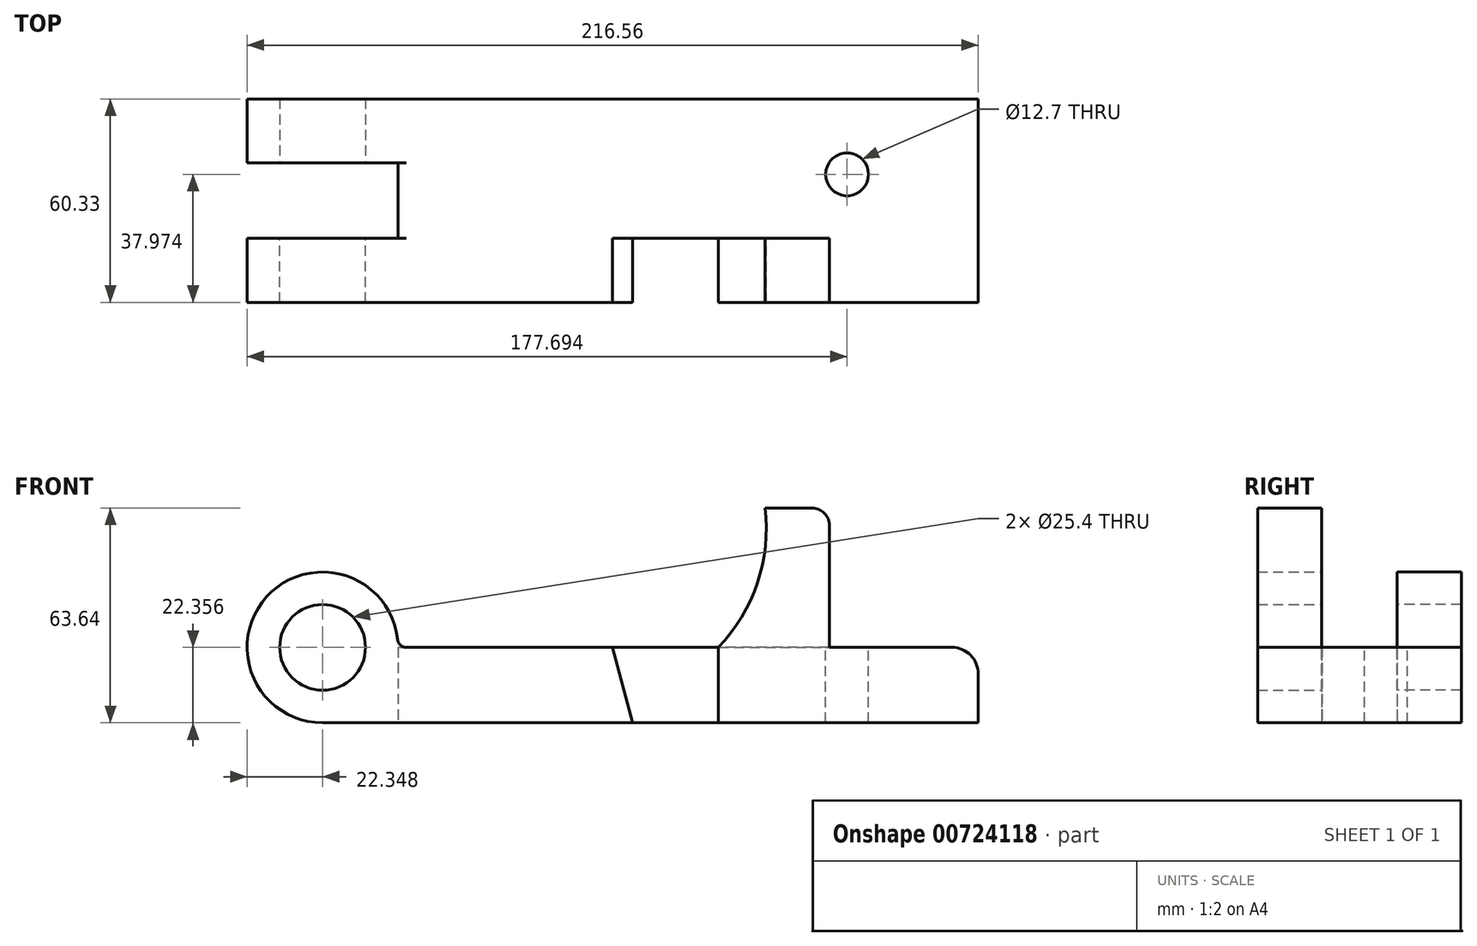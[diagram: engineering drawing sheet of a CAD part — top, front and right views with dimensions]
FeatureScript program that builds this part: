
annotation { "Feature Type Name" : "Feature", "Feature Type Description" : "" }
export const myFeature = defineFeature(function(context is Context, id is Id, definition is map)
    precondition{}
    {
        {
            var Q0;
            Q0=qCreatedBy(makeId("Front.planeOp"),FACE);
            var sketch = newSketch(context, id + "F0", { "sketchPlane" : qUnion([Q0])});
            skLineSegment(sketch, "E0.bottom", {"start": v(-66.8, 11.18) * mm, "end": v(79.5, 11.18) * mm});
            skLineSegment(sketch, "E0.top", {"start": v(-79.5, -11.18) * mm, "end": v(79.5, -11.18) * mm});
            skLineSegment(sketch, "E0.left", {"start": v(-79.5, -1.52) * mm, "end": v(-79.5, -11.18) * mm});
            skPoint(sketch, "E0.middle", {"position": v(0, 0) * mm});
            skArc(sketch, "E1", {"start": v(-57.15, 11.18) * mm, "mid": v(-95.3, 26.98) * mm, "end": v(-79.5, -11.18) * mm});
            skCircle(sketch, "E2", {"center": v(-79.5, 11.18) * mm, "radius": 12.7 * mm});
            skLineSegment(sketch, "E3", {"start": v(-79.5, -1.52) * mm, "end": v(-79.5, 11.18) * mm, "construction": true});
            skArc(sketch, "E4", {"start": v(-79.5, -11.18) * mm, "mid": v(-63.7, -4.63) * mm, "end": v(-57.15, 11.18) * mm});
            skLineSegment(sketch, "E5", {"start": v(6.35, 11.18) * mm, "end": v(12.34, -11.18) * mm});
            skLineSegment(sketch, "E6", {"start": v(37.74, 11.18) * mm, "end": v(37.74, -11.18) * mm});
            skLineSegment(sketch, "E7.bottom", {"start": v(37.74, 11.18) * mm, "end": v(70.59, 11.18) * mm});
            skLineSegment(sketch, "E7.right", {"start": v(70.59, 11.18) * mm, "end": v(70.59, 52.46) * mm});
            skLineSegment(sketch, "E8", {"start": v(79.5, 11.18) * mm, "end": v(114.7, 11.18) * mm});
            skLineSegment(sketch, "E9", {"start": v(114.7, 11.18) * mm, "end": v(114.7, -11.18) * mm});
            skLineSegment(sketch, "E10", {"start": v(114.7, -11.18) * mm, "end": v(79.5, -11.18) * mm});
            skPoint(sketch, "E11", {"position": v(-101.85, 11.18) * mm});
            skLineSegment(sketch, "E12", {"start": v(70.59, 52.46) * mm, "end": v(51.54, 52.46) * mm});
            skArc(sketch, "E13", {"start": v(37.74, 11.18) * mm, "mid": v(49.29, 30.26) * mm, "end": v(51.54, 52.46) * mm});
            skSolve(sketch);
        }
        {
            var Q0;
            Q0 = qSketchRegion(id + "F0", true);
            extrude(context, id + "F1", {"entities" : qUnion([Q0]), "depth" : 19 * mm, "offsetDistance" : 25.4 * mm});
        }
        {
            var Q0;
            {var subQ0=sQuery(id+"F0.wireOp",EDGE,"E4");Q0=makeQuery(id+"F0.imprint","IMPRINT",FACE,{"disambiguationData":[TD([[makeQuery(id+"F0.imprint","IMPRINT",EDGE,{"derivedFrom":subQ0}),-1.0]])]});}
            var sketch = newSketch(context, id + "F2", { "sketchPlane" : qUnion([Q0])});
            skLineSegment(sketch, "E14.bottom", {"start": v(114.7, 11.18) * mm, "end": v(-57.17, 11.18) * mm});
            skLineSegment(sketch, "E14.top", {"start": v(114.7, -11.17) * mm, "end": v(-57.17, -11.17) * mm});
            skLineSegment(sketch, "E14.left", {"start": v(114.7, 11.18) * mm, "end": v(114.7, -11.17) * mm});
            skLineSegment(sketch, "E14.right", {"start": v(-57.17, 11.18) * mm, "end": v(-57.17, -11.17) * mm});
            skSolve(sketch);
        }
        {
            var Q0;
            Q0 = qSketchRegion(id + "F2", true);
            extrude(context, id + "F3", {"entities" : qUnion([Q0]), "operationType" : NewBodyOperationType.ADD, "oppositeDirection" : true, "depth" : 11.16 * mm, "offsetDistance" : 25.4 * mm});
        }
        {
            var Q0;
            Q0=makeQuery(id+"F3.opExtrude","CAP_FACE",FACE,{"disambiguationData":[OSD([sQuery(id+"F2.wireOp",EDGE,"E14.bottom"),sQuery(id+"F2.wireOp",EDGE,"E14.top"),sQuery(id+"F2.wireOp",EDGE,"E14.left"),sQuery(id+"F2.wireOp",EDGE,"E14.right")])],"isStart":false});
            cPlane(context, id + "F4", {"entities" : qUnion([Q0]), "cplaneType" : CPlaneType.OFFSET, "offset" : 0 * mm, "width" : 152.4 * mm, "height" : 152.4 * mm});
        }
        {
            var Q0;
            Q0=makeQuery(id+"F1.opExtrude","SWEPT_BODY",BODY,{"disambiguationData":[OSD([sQuery(id+"F0.wireOp",EDGE,"E0.bottom"),sQuery(id+"F0.wireOp",EDGE,"E0.top"),sQuery(id+"F0.wireOp",EDGE,"E1"),sQuery(id+"F0.wireOp",EDGE,"E2"),sQuery(id+"F0.wireOp",EDGE,"E7.right"),sQuery(id+"F0.wireOp",EDGE,"E8"),sQuery(id+"F0.wireOp",EDGE,"E9"),sQuery(id+"F0.wireOp",EDGE,"E10"),sQuery(id+"F0.wireOp",EDGE,"E12"),sQuery(id+"F0.wireOp",EDGE,"E13")])]});
            var Q1;
            Q1=makeQuery(id+"F3.opExtrude","SWEPT_BODY",BODY,{"disambiguationData":[OSD([sQuery(id+"F2.wireOp",EDGE,"E14.bottom"),sQuery(id+"F2.wireOp",EDGE,"E14.top"),sQuery(id+"F2.wireOp",EDGE,"E14.left"),sQuery(id+"F2.wireOp",EDGE,"E14.right")])]});
            var Q2;
            Q2=qCreatedBy(id+"F4.planeOp",FACE);
            mirror(context, id + "F5", {"operationType" : NewBodyOperationType.ADD, "entities" : qUnion([Q0, Q1]), "mirrorPlane" : qUnion([Q2])});
        }
        {
            var Q0;
            Q0=makeQuery(id+"F5.opPattern","COPY",FACE,{"derivedFrom":makeQuery(id+"F1.opExtrude","CAP_FACE",FACE,{"disambiguationData":[OSD([sQuery(id+"F0.wireOp",EDGE,"E0.bottom"),sQuery(id+"F0.wireOp",EDGE,"E0.top"),sQuery(id+"F0.wireOp",EDGE,"E1"),sQuery(id+"F0.wireOp",EDGE,"E2"),sQuery(id+"F0.wireOp",EDGE,"E7.right"),sQuery(id+"F0.wireOp",EDGE,"E8"),sQuery(id+"F0.wireOp",EDGE,"E9"),sQuery(id+"F0.wireOp",EDGE,"E10"),sQuery(id+"F0.wireOp",EDGE,"E12"),sQuery(id+"F0.wireOp",EDGE,"E13")])],"isStart":false}),"instanceName":"1"});
            var sketch = newSketch(context, id + "F6", { "sketchPlane" : qUnion([Q0])});
            skLineSegment(sketch, "E15.bottom", {"start": v(-70.59, 52.46) * mm, "end": v(-34.03, 52.46) * mm});
            skLineSegment(sketch, "E15.top", {"start": v(-70.59, 11.18) * mm, "end": v(-34.03, 11.18) * mm});
            skLineSegment(sketch, "E15.left", {"start": v(-70.59, 52.46) * mm, "end": v(-70.59, 11.18) * mm});
            skLineSegment(sketch, "E15.right", {"start": v(-34.03, 52.46) * mm, "end": v(-34.03, 11.18) * mm});
            skSolve(sketch);
        }
        {
            var Q0;
            Q0 = qSketchRegion(id + "F6", true);
            extrude(context, id + "F7", {"entities" : qUnion([Q0]), "operationType" : NewBodyOperationType.REMOVE, "oppositeDirection" : true, "depth" : 25.4 * mm, "offsetDistance" : 25.4 * mm});
        }
        {
            var Q0;
            Q0=makeQuery(id+"F1.opExtrude","SWEPT_EDGE",EDGE,{"disambiguationData":[OSD([sQuery(id+"F0.wireOp",EDGE,"E7.right"),sQuery(id+"F0.wireOp",EDGE,"E12")])]});
            fillet(context, id + "F8", {"entities" : qUnion([Q0]), "radius" : 5.08 * mm, "tangentPropagation" : true, "allowEdgeOverflow" : false});
        }
        {
            var Q0;
            Q0=makeQuery(id+"F5.opPattern","COPY",EDGE,{"derivedFrom":makeQuery(id+"F1.opExtrude","SWEPT_EDGE",EDGE,{"disambiguationData":[OSD([sQuery(id+"F0.wireOp",EDGE,"E8"),sQuery(id+"F0.wireOp",EDGE,"E9")])]}),"instanceName":"1"});
            fillet(context, id + "F9", {"entities" : qUnion([Q0]), "radius" : 7.87 * mm, "tangentPropagation" : true, "allowEdgeOverflow" : false});
        }
        {
            var Q0;
            Q0=makeQuery(id+"F1.opExtrude","SWEPT_EDGE",EDGE,{"disambiguationData":[OSD([sQuery(id+"F0.wireOp",EDGE,"E0.bottom"),sQuery(id+"F0.wireOp",EDGE,"E1"),sQuery(id+"F0.wireOp",EDGE,"E4")])]});
            fillet(context, id + "F10", {"entities" : qUnion([Q0]), "radius" : 2.54 * mm, "tangentPropagation" : true, "allowEdgeOverflow" : false});
        }
        {
            var Q0;
            Q0=makeQuery(id+"F5.opPattern","COPY",EDGE,{"derivedFrom":makeQuery(id+"F1.opExtrude","SWEPT_EDGE",EDGE,{"disambiguationData":[OSD([sQuery(id+"F0.wireOp",EDGE,"E0.bottom"),sQuery(id+"F0.wireOp",EDGE,"E1"),sQuery(id+"F0.wireOp",EDGE,"E4")])]}),"instanceName":"1"});
            fillet(context, id + "F11", {"entities" : qUnion([Q0]), "radius" : 2.54 * mm, "tangentPropagation" : true, "allowEdgeOverflow" : false});
        }
        {
            var Q0;
            Q0=makeQuery(id+"F1.opExtrude","CAP_FACE",FACE,{"disambiguationData":[OSD([sQuery(id+"F0.wireOp",EDGE,"E0.bottom"),sQuery(id+"F0.wireOp",EDGE,"E0.top"),sQuery(id+"F0.wireOp",EDGE,"E1"),sQuery(id+"F0.wireOp",EDGE,"E2"),sQuery(id+"F0.wireOp",EDGE,"E7.right"),sQuery(id+"F0.wireOp",EDGE,"E8"),sQuery(id+"F0.wireOp",EDGE,"E9"),sQuery(id+"F0.wireOp",EDGE,"E10"),sQuery(id+"F0.wireOp",EDGE,"E12"),sQuery(id+"F0.wireOp",EDGE,"E13")])],"isStart":false});
            var sketch = newSketch(context, id + "F12", { "sketchPlane" : qUnion([Q0])});
            skLineSegment(sketch, "E16", {"start": v(12.34, -11.18) * mm, "end": v(37.74, -11.18) * mm});
            skLineSegment(sketch, "E17", {"start": v(37.74, -11.18) * mm, "end": v(37.74, 11.18) * mm});
            skLineSegment(sketch, "E18", {"start": v(37.74, 11.18) * mm, "end": v(6.35, 11.18) * mm});
            skLineSegment(sketch, "E19", {"start": v(6.35, 11.18) * mm, "end": v(12.34, -11.18) * mm});
            skSolve(sketch);
        }
        {
            var Q0;
            Q0 = qSketchRegion(id + "F12", true);
            extrude(context, id + "F13", {"entities" : qUnion([Q0]), "operationType" : NewBodyOperationType.REMOVE, "oppositeDirection" : true, "depth" : 19.05 * mm, "offsetDistance" : 25.4 * mm});
        }
        {
            var Q0;
            {var subQ0=sQuery(id+"F0.wireOp",EDGE,"E0.bottom");Q0=makeQuery(id+"F7.boolean.opBoolean","MERGE",FACE,{"derivedFrom":[makeQuery(id+"F5.opPattern","COPY",FACE,{"derivedFrom":makeQuery(id+"F1.opExtrude","SWEPT_FACE",FACE,{"disambiguationData":[OSD([subQ0])]}),"instanceName":"1"}),makeQuery(id+"F5.opPattern","COPY",FACE,{"derivedFrom":makeQuery(id+"F1.opExtrude","SWEPT_FACE",FACE,{"disambiguationData":[OSD([subQ0,sQuery(id+"F0.wireOp",EDGE,"E8")])]}),"instanceName":"1"}),makeQuery(id+"F7.opExtrude","SWEPT_FACE",FACE,{"disambiguationData":[OSD([sQuery(id+"F6.wireOp",EDGE,"E15.top")])]})]});}
            var sketch = newSketch(context, id + "F14", { "sketchPlane" : qUnion([Q0])});
            skCircle(sketch, "E20", {"center": v(75.84, 18.97) * mm, "radius": 6.35 * mm});
            skPoint(sketch, "E20.centerSnap0", {"position": v(135.81, 18.97) * mm});
            skSolve(sketch);
        }
        {
            var Q0;
            Q0 = qSketchRegion(id + "F14", true);
            extrude(context, id + "F15", {"entities" : qUnion([Q0]), "operationType" : NewBodyOperationType.REMOVE, "oppositeDirection" : true, "depth" : 71.88 * mm, "offsetDistance" : 25.4 * mm});
        }
    });
